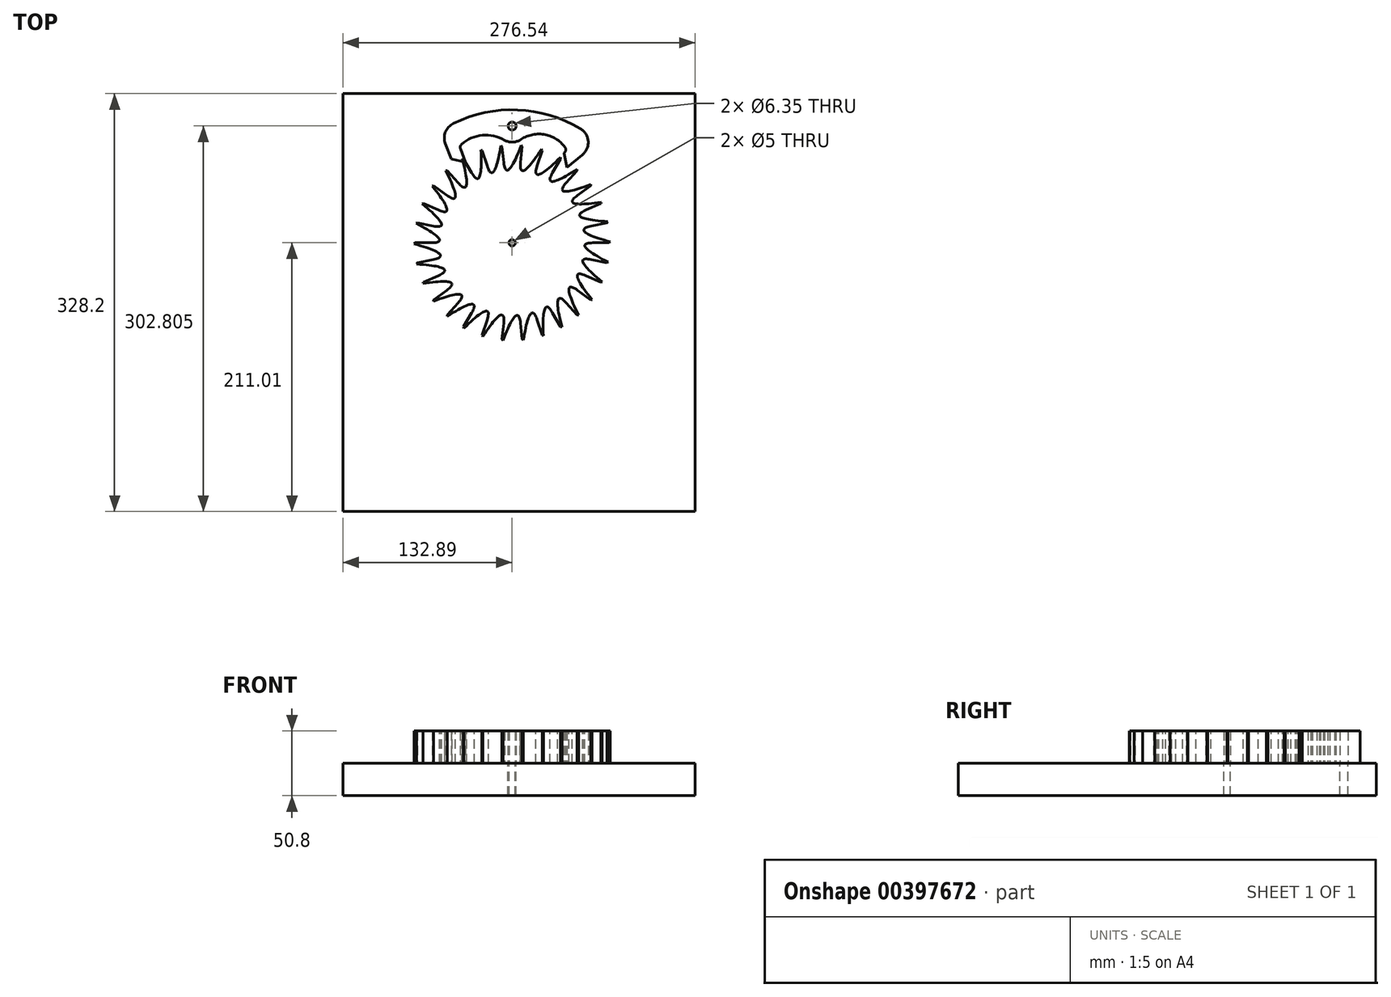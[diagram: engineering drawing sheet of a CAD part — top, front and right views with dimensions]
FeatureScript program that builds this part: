
annotation { "Feature Type Name" : "Feature", "Feature Type Description" : "" }
export const myFeature = defineFeature(function(context is Context, id is Id, definition is map)
    precondition{}
    {
        {
            var Q0;
            Q0=qCreatedBy(makeId("Top.planeOp"),FACE);
            var sketch = newSketch(context, id + "F0", { "sketchPlane" : qUnion([Q0])});
            skCircle(sketch, "E0", {"center": v(0, 0) * mm, "radius": 76.2 * mm, "construction": true});
            skCircle(sketch, "E1", {"center": v(0, 0) * mm, "radius": 95.25 * mm, "construction": true});
            skCircle(sketch, "E2", {"center": v(0, 0) * mm, "radius": 57.15 * mm, "construction": true});
            skLineSegment(sketch, "E3", {"start": v(0, 0) * mm, "end": v(-38.48, 66.66) * mm, "construction": true});
            skLineSegment(sketch, "E4", {"start": v(-104.67, 27.56) * mm, "end": v(65.84, 126) * mm, "construction": true});
            skLineSegment(sketch, "E5", {"start": v(0, 0) * mm, "end": v(-38.24, 42.47) * mm, "construction": true});
            skLineSegment(sketch, "E6", {"start": v(-96.61, 34.43) * mm, "end": v(96.61, 141.54) * mm, "construction": true});
            skPoint(sketch, "E7", {"position": v(0, 87.99) * mm});
            skPoint(sketch, "E7.positionSnap0", {"position": v(0, 87.99) * mm});
            skLineSegment(sketch, "E8", {"start": v(-38.1, 66) * mm, "end": v(-39.17, 66.28) * mm});
            skPoint(sketch, "E9", {"position": v(-42.49, 47.19) * mm});
            skPoint(sketch, "E10", {"position": v(-37.64, 60.11) * mm});
            skLineSegment(sketch, "E11.trimOffspring", {"start": v(-40.07, 69.4) * mm, "end": v(-47.63, 82.49) * mm});
            skEllipticalArc(sketch, "E12.trimOffspring", {});
            skLineSegment(sketch, "E13.trimOffspring", {"start": v(-42.49, 47.19) * mm, "end": v(-50.99, 56.63) * mm});
            skCircle(sketch, "E14", {"center": v(0, 0) * mm, "radius": 2.5 * mm});
            skLineSegment(sketch, "E15", {"start": v(0, 0) * mm, "end": v(61, 105.66) * mm, "construction": true});
            skLineSegment(sketch, "E16.1.0", {"start": v(-50.99, 56.63) * mm, "end": v(-52.1, 56.69) * mm});
            skEllipticalArc(sketch, "E16.1.1", {});
            skLineSegment(sketch, "E16.1.2", {"start": v(-51.37, 37.32) * mm, "end": v(-61.65, 44.79) * mm});
            skLineSegment(sketch, "E16.2.0", {"start": v(-61.65, 44.79) * mm, "end": v(-62.74, 44.62) * mm});
            skEllipticalArc(sketch, "E16.2.1", {});
            skLineSegment(sketch, "E16.2.2", {"start": v(-58.01, 25.83) * mm, "end": v(-69.61, 31) * mm});
            skEllipticalArc(sketch, "E17.3.3.0", {});
            skLineSegment(sketch, "E17.7.3.0", {"start": v(-62.11, 13.2) * mm, "end": v(-74.53, 15.84) * mm});
            skLineSegment(sketch, "E17.9.3.0", {"start": v(-69.61, 31) * mm, "end": v(-70.64, 30.6) * mm});
            skEllipticalArc(sketch, "E17.3.4.0", {});
            skLineSegment(sketch, "E17.7.4.0", {"start": v(-63.5, 0) * mm, "end": v(-76.2, 0) * mm});
            skLineSegment(sketch, "E17.9.4.0", {"start": v(-74.53, 15.84) * mm, "end": v(-75.46, 15.24) * mm});
            skEllipticalArc(sketch, "E17.3.5.0", {});
            skLineSegment(sketch, "E17.7.5.0", {"start": v(-62.11, -13.2) * mm, "end": v(-74.53, -15.84) * mm});
            skLineSegment(sketch, "E17.9.5.0", {"start": v(-76.2, 0) * mm, "end": v(-76.98, -0.78) * mm});
            skEllipticalArc(sketch, "E17.3.6.0", {});
            skLineSegment(sketch, "E17.7.6.0", {"start": v(-58.01, -25.83) * mm, "end": v(-69.61, -31) * mm});
            skLineSegment(sketch, "E17.9.6.0", {"start": v(-74.53, -15.84) * mm, "end": v(-75.14, -16.77) * mm});
            skEllipticalArc(sketch, "E17.3.7.0", {});
            skLineSegment(sketch, "E17.7.7.0", {"start": v(-51.37, -37.32) * mm, "end": v(-61.65, -44.79) * mm});
            skLineSegment(sketch, "E17.9.7.0", {"start": v(-69.61, -31) * mm, "end": v(-70, -32.03) * mm});
            skEllipticalArc(sketch, "E17.3.8.0", {});
            skLineSegment(sketch, "E17.7.8.0", {"start": v(-42.49, -47.19) * mm, "end": v(-50.99, -56.63) * mm});
            skLineSegment(sketch, "E17.9.8.0", {"start": v(-61.65, -44.79) * mm, "end": v(-61.82, -45.88) * mm});
            skEllipticalArc(sketch, "E17.3.9.0", {});
            skLineSegment(sketch, "E17.7.9.0", {"start": v(-31.75, -55) * mm, "end": v(-38.1, -66) * mm});
            skLineSegment(sketch, "E17.9.9.0", {"start": v(-50.99, -56.63) * mm, "end": v(-50.93, -57.73) * mm});
            skEllipticalArc(sketch, "E17.3.10.0", {});
            skLineSegment(sketch, "E17.7.10.0", {"start": v(-19.62, -60.4) * mm, "end": v(-23.55, -72.47) * mm});
            skLineSegment(sketch, "E17.9.10.0", {"start": v(-38.1, -66) * mm, "end": v(-37.81, -67.06) * mm});
            skEllipticalArc(sketch, "E17.3.11.0", {});
            skLineSegment(sketch, "E17.7.11.0", {"start": v(-6.64, -63.15) * mm, "end": v(-7.97, -75.78) * mm});
            skLineSegment(sketch, "E17.9.11.0", {"start": v(-23.55, -72.47) * mm, "end": v(-23.05, -73.46) * mm});
            skEllipticalArc(sketch, "E17.3.12.0", {});
            skLineSegment(sketch, "E17.7.12.0", {"start": v(6.64, -63.15) * mm, "end": v(7.97, -75.78) * mm});
            skLineSegment(sketch, "E17.9.12.0", {"start": v(-7.97, -75.78) * mm, "end": v(-7.27, -76.64) * mm});
            skEllipticalArc(sketch, "E17.3.13.0", {});
            skLineSegment(sketch, "E17.7.13.0", {"start": v(19.62, -60.4) * mm, "end": v(23.55, -72.47) * mm});
            skLineSegment(sketch, "E17.9.13.0", {"start": v(7.97, -75.78) * mm, "end": v(8.82, -76.48) * mm});
            skEllipticalArc(sketch, "E17.3.14.0", {});
            skLineSegment(sketch, "E17.7.14.0", {"start": v(31.75, -55) * mm, "end": v(38.1, -66) * mm});
            skLineSegment(sketch, "E17.9.14.0", {"start": v(23.55, -72.47) * mm, "end": v(24.53, -72.97) * mm});
            skEllipticalArc(sketch, "E18.3.15.0", {});
            skLineSegment(sketch, "E18.7.15.0", {"start": v(42.49, -47.19) * mm, "end": v(50.99, -56.63) * mm});
            skLineSegment(sketch, "E18.9.15.0", {"start": v(38.1, -66) * mm, "end": v(39.17, -66.28) * mm});
            skEllipticalArc(sketch, "E18.3.16.0", {});
            skLineSegment(sketch, "E18.7.16.0", {"start": v(51.37, -37.32) * mm, "end": v(61.65, -44.79) * mm});
            skLineSegment(sketch, "E18.9.16.0", {"start": v(50.99, -56.63) * mm, "end": v(52.1, -56.69) * mm});
            skEllipticalArc(sketch, "E18.3.17.0", {});
            skLineSegment(sketch, "E18.7.17.0", {"start": v(58.01, -25.83) * mm, "end": v(69.61, -31) * mm});
            skLineSegment(sketch, "E18.9.17.0", {"start": v(61.65, -44.79) * mm, "end": v(62.74, -44.62) * mm});
            skEllipticalArc(sketch, "E18.3.18.0", {});
            skLineSegment(sketch, "E18.7.18.0", {"start": v(62.11, -13.2) * mm, "end": v(74.53, -15.84) * mm});
            skLineSegment(sketch, "E18.9.18.0", {"start": v(69.61, -31) * mm, "end": v(70.64, -30.6) * mm});
            skEllipticalArc(sketch, "E18.3.19.0", {});
            skLineSegment(sketch, "E18.7.19.0", {"start": v(63.5, 0) * mm, "end": v(76.2, 0) * mm});
            skLineSegment(sketch, "E18.9.19.0", {"start": v(74.53, -15.84) * mm, "end": v(75.46, -15.24) * mm});
            skEllipticalArc(sketch, "E18.3.20.0", {});
            skLineSegment(sketch, "E18.7.20.0", {"start": v(62.11, 13.2) * mm, "end": v(74.53, 15.84) * mm});
            skLineSegment(sketch, "E18.9.20.0", {"start": v(76.2, 0) * mm, "end": v(76.98, 0.78) * mm});
            skEllipticalArc(sketch, "E18.3.21.0", {});
            skLineSegment(sketch, "E18.7.21.0", {"start": v(58.01, 25.83) * mm, "end": v(69.61, 31) * mm});
            skLineSegment(sketch, "E18.9.21.0", {"start": v(74.53, 15.84) * mm, "end": v(75.14, 16.77) * mm});
            skEllipticalArc(sketch, "E18.3.22.0", {});
            skLineSegment(sketch, "E18.7.22.0", {"start": v(51.37, 37.32) * mm, "end": v(61.65, 44.79) * mm});
            skLineSegment(sketch, "E18.9.22.0", {"start": v(69.61, 31) * mm, "end": v(70, 32.03) * mm});
            skEllipticalArc(sketch, "E18.3.23.0", {});
            skLineSegment(sketch, "E18.7.23.0", {"start": v(42.49, 47.19) * mm, "end": v(50.99, 56.63) * mm});
            skLineSegment(sketch, "E18.9.23.0", {"start": v(61.65, 44.79) * mm, "end": v(61.82, 45.88) * mm});
            skEllipticalArc(sketch, "E18.3.24.0", {});
            skLineSegment(sketch, "E18.7.24.0", {"start": v(31.75, 55) * mm, "end": v(38.1, 66) * mm});
            skLineSegment(sketch, "E18.9.24.0", {"start": v(50.99, 56.63) * mm, "end": v(50.93, 57.73) * mm});
            skEllipticalArc(sketch, "E18.3.25.0", {});
            skLineSegment(sketch, "E18.7.25.0", {"start": v(19.62, 60.4) * mm, "end": v(23.55, 72.47) * mm});
            skLineSegment(sketch, "E18.9.25.0", {"start": v(38.1, 66) * mm, "end": v(37.81, 67.06) * mm});
            skEllipticalArc(sketch, "E18.3.26.0", {});
            skLineSegment(sketch, "E18.7.26.0", {"start": v(6.64, 63.15) * mm, "end": v(7.97, 75.78) * mm});
            skLineSegment(sketch, "E18.9.26.0", {"start": v(23.55, 72.47) * mm, "end": v(23.05, 73.46) * mm});
            skEllipticalArc(sketch, "E18.3.27.0", {});
            skLineSegment(sketch, "E18.7.27.0", {"start": v(-6.64, 63.15) * mm, "end": v(-7.97, 75.78) * mm});
            skLineSegment(sketch, "E18.9.27.0", {"start": v(7.97, 75.78) * mm, "end": v(7.27, 76.64) * mm});
            skEllipticalArc(sketch, "E18.3.28.0", {});
            skLineSegment(sketch, "E18.7.28.0", {"start": v(-19.62, 60.4) * mm, "end": v(-23.55, 72.47) * mm});
            skLineSegment(sketch, "E18.9.28.0", {"start": v(-7.97, 75.78) * mm, "end": v(-8.82, 76.48) * mm});
            skEllipticalArc(sketch, "E18.3.29.0", {});
            skLineSegment(sketch, "E18.7.29.0", {"start": v(-31.75, 55) * mm, "end": v(-38.1, 66) * mm});
            skLineSegment(sketch, "E18.9.29.0", {"start": v(-23.55, 72.47) * mm, "end": v(-24.53, 72.97) * mm});
            const initialGuessF0  = {"E12.trimOffspring": [-0.16816268729673498, 0.34113311566798743, 0.40352375597021906, -0.9149691679874722, 0.32512873879015974, 0.019857114403106217, 6.099533507210712, 0.36648975676927714], "E16.1.1": [-0.23541349198471206, 0.29871554997316746, 0.5849385805037574, -0.8110775900234511, 0.32512873879015974, 0.019857114403106217, 6.0995335072107135, 0.3664897567692766], "E16.2.1": [-0.29237559743369124, 0.2432426813482785, 0.7407887822225573, -0.6717380293933201, 0.32512873879015974, 0.019857114403106217, 6.099533507210716, 0.36648975676927575], "E17.3.3.0": [-0.3365594863010441, 0.17713894034058497, 0.864262959459267, -0.5030402935220094, 0.32512873879015974, 0.019857114403106217, 6.0995335072107135, 0.36648975676927664], "E17.3.4.0": [-0.3660341106254456, 0.1032933776330654, 0.9499646981738034, -0.31235728296864607, 0.32512873879015974, 0.019857114403106217, 6.099533507210712, 0.366489756769277], "E17.3.5.0": [-0.3795112878889799, 0.024933398666362776, 0.994148421141772, -0.108022760293014, 0.32512873879015974, 0.019857114403106217, 6.099533507210712, 0.3664897567692774], "E17.3.6.0": [-0.3764020007745591, -0.05451628946578102, 0.9948830876524474, 0.10103287535813742, 0.32512873879015974, 0.019857114403106217, 6.099533507210713, 0.36648975676927614], "E17.3.7.0": [-0.35684214004909803, -0.1315833541500894, 0.9521365892539916, 0.30567288954661254, 0.32512873879015974, 0.019857114403106217, 6.09953350721071, 0.36648975676927764], "E17.3.8.0": [-0.3216865654849248, -0.20289959485105222, 0.8677771530468744, 0.49695353168064077, 0.32512873879015974, 0.019857114403106217, 6.099533507210713, 0.36648975676927675], "E17.3.9.0": [-0.2724717443856568, -0.26534814963674647, 0.7454916911948335, 0.6665149198326074, 0.32512873879015974, 0.019857114403106217, 6.099533507210709, 0.3664897567692777], "E17.3.10.0": [-0.21134860059224522, -0.3161997170016246, 0.5906246651715533, 0.806946407694458, 0.32512873879015974, 0.019857114403106217, 6.099533507210708, 0.3664897567692784], "E17.3.11.0": [-0.1409885087898473, -0.3532318394389483, 0.40994450714869024, 0.9121104653815882, 0.32512873879015974, 0.019857114403106217, 6.099533507210709, 0.3664897567692783], "E17.3.12.0": [-0.0644665426154071, -0.37482603549836785, 0.21134780703143413, 0.9774109189399328, 0.32512873879015974, 0.019857114403106217, 6.099533507210708, 0.36648975676927825], "E17.3.13.0": [0.014872920816119035, -0.38003853519163716, 0.0035141935876077833, 0.9999938252026503, 0.32512873879015974, 0.019857114403106217, 6.099533507210706, 0.36648975676927936], "E17.3.14.0": [0.09356236623978852, -0.36864152726981186, -0.20447300697896975, 0.9788722028012534, 0.32512873879015974, 0.019857114403106217, 6.099533507210706, 0.3664897567692789], "E18.3.15.0": [0.16816268729673456, -0.34113311566798726, -0.4035237559702191, 0.9149691679874721, 0.32512873879015974, 0.019857114403106217, 6.0995335072107055, 0.3664897567692796], "E18.3.16.0": [0.2354134919847116, -0.2987155499731673, -0.5849385805037571, 0.8110775900234511, 0.32512873879015974, 0.019857114403106217, 6.099533507210705, 0.3664897567692797], "E18.3.17.0": [0.2923755974336907, -0.2432426813482784, -0.7407887822225572, 0.6717380293933201, 0.32512873879015974, 0.019857114403106214, 6.099533507210705, 0.36648975676928064], "E18.3.18.0": [0.3365594863010437, -0.17713894034058492, -0.8642629594592669, 0.5030402935220095, 0.32512873879015974, 0.019857114403106217, 6.099533507210706, 0.36648975676927975], "E18.3.19.0": [0.36603411062544516, -0.10329337763306534, -0.9499646981738034, 0.31235728296864623, 0.32512873879015974, 0.019857114403106217, 6.099533507210705, 0.3664897567692802], "E18.3.20.0": [0.37951128788897953, -0.02493339866636276, -0.9941484211417722, 0.10802276029301414, 0.32512873879015974, 0.019857114403106217, 6.0995335072107055, 0.36648975676928014], "E18.3.21.0": [0.37640200077455865, 0.05451628946578116, -0.9948830876524474, -0.10103287535813729, 0.32512873879015974, 0.019857114403106217, 6.099533507210706, 0.3664897567692802], "E18.3.22.0": [0.35684214004909776, 0.13158335415008934, -0.9521365892539917, -0.3056728895466124, 0.32512873879015974, 0.019857114403106217, 6.0995335072107055, 0.36648975676928003], "E18.3.23.0": [0.32168656548492447, 0.20289959485105225, -0.8677771530468744, -0.4969535316806406, 0.32512873879015974, 0.019857114403106217, 6.099533507210707, 0.3664897567692799], "E18.3.24.0": [0.2724717443856564, 0.26534814963674663, -0.7454916911948336, -0.6665149198326072, 0.32512873879015974, 0.019857114403106217, 6.099533507210708, 0.36648975676928003], "E18.3.25.0": [0.211348600592245, 0.31619971700162464, -0.5906246651715534, -0.806946407694458, 0.32512873879015974, 0.019857114403106217, 6.099533507210707, 0.36648975676927903], "E18.3.26.0": [0.14098850878984698, 0.35323183943894854, -0.4099445071486904, -0.9121104653815882, 0.32512873879015974, 0.019857114403106217, 6.099533507210711, 0.36648975676927825], "E18.3.27.0": [0.06446654261540674, 0.374826035498368, -0.21134780703143421, -0.9774109189399326, 0.32512873879015974, 0.019857114403106217, 6.099533507210711, 0.36648975676927875], "E18.3.28.0": [-0.01487292081611923, 0.3800385351916374, -0.0035141935876079056, -0.9999938252026503, 0.32512873879015974, 0.019857114403106217, 6.099533507210711, 0.36648975676927703], "E18.3.29.0": [-0.09356236623978904, 0.368641527269812, 0.20447300697896967, -0.9788722028012535, 0.32512873879015974, 0.019857114403106217, 6.099533507210712, 0.36648975676927786]};
            skSetInitialGuess(sketch, initialGuessF0);
            skSolve(sketch);
        }
        {
            var Q0;
            Q0=qSketchRegion(id+"F0",true);
            extrude(context, id + "F1", {"entities" : qUnion([Q0]), "depth" : 25.4 * mm});
        }
        {
            var Q0;
            Q0=qCreatedBy(makeId("Top.planeOp"),FACE);
            var sketch = newSketch(context, id + "F2", { "sketchPlane" : qUnion([Q0])});
            skLineSegment(sketch, "E19", {"start": v(0, 0) * mm, "end": v(-100.8, 155.22) * mm, "construction": true});
            skLineSegment(sketch, "E20", {"start": v(0, 0) * mm, "end": v(100.8, 155.22) * mm, "construction": true});
            skLineSegment(sketch, "E21", {"start": v(0, 0) * mm, "end": v(-108.35, 149.14) * mm, "construction": true});
            skLineSegment(sketch, "E22", {"start": v(0, 0) * mm, "end": v(-92.17, 159.65) * mm, "construction": true});
            skLineSegment(sketch, "E23", {"start": v(0, 0) * mm, "end": v(86.35, 149.56) * mm, "construction": true});
            skLineSegment(sketch, "E24", {"start": v(0, 0) * mm, "end": v(101.51, 139.72) * mm, "construction": true});
            skCircle(sketch, "E25", {"center": v(0, 0) * mm, "radius": 76.99 * mm, "construction": true});
            skPoint(sketch, "E26.0", {"position": v(-8.82, 76.48) * mm});
            skLineSegment(sketch, "E27", {"start": v(-41.93, 64.57) * mm, "end": v(0, 91.8) * mm, "construction": true});
            skLineSegment(sketch, "E28", {"start": v(0, 91.8) * mm, "end": v(41.93, 64.57) * mm, "construction": true});
            skLineSegment(sketch, "E29", {"start": v(-47.82, 65.82) * mm, "end": v(-36.63, 63.44) * mm});
            skLineSegment(sketch, "E30", {"start": v(40.68, 70.46) * mm, "end": v(43.06, 59.26) * mm});
            skCircle(sketch, "E31", {"center": v(0, 91.8) * mm, "radius": 3.18 * mm});
            skLineSegment(sketch, "E32", {"start": v(-47.82, 65.82) * mm, "end": v(-52.42, 77.8) * mm});
            skLineSegment(sketch, "E33", {"start": v(43.06, 59.26) * mm, "end": v(55.03, 68.96) * mm});
            skLineSegment(sketch, "E34", {"start": v(40.68, 70.46) * mm, "end": v(40.94, 70.67) * mm});
            skLineSegment(sketch, "E35", {"start": v(-36.63, 63.44) * mm, "end": v(-40.61, 73.82) * mm});
            skArc(sketch, "E36", {"start": v(53.54, 89.73) * mm, "mid": v(4.2, 104.41) * mm, "end": v(-46.17, 93.74) * mm});
            skArc(sketch, "E37", {"start": v(-5.99, 80.6) * mm, "mid": v(0, 79.1) * mm, "end": v(5.99, 80.6) * mm});
            skArc(sketch, "E38.trimOffspring", {"start": v(-5.99, 80.6) * mm, "mid": v(-23.42, 84.52) * mm, "end": v(-39.77, 77.32) * mm});
            skArc(sketch, "E39.trimOffspring", {"start": v(41.51, 75) * mm, "mid": v(24.9, 85.16) * mm, "end": v(5.99, 80.6) * mm});
            skPoint(sketch, "E40.visualSharp", {"position": v(-56.34, 88) * mm});
            skArc(sketch, "E40.filletArc", {"start": v(-46.17, 93.74) * mm, "mid": v(-52.39, 86.98) * mm, "end": v(-52.42, 77.8) * mm});
            skPoint(sketch, "E41.visualSharp", {"position": v(67.93, 79.4) * mm});
            skArc(sketch, "E41.filletArc", {"start": v(55.03, 68.96) * mm, "mid": v(59.7, 79.73) * mm, "end": v(53.54, 89.73) * mm});
            skPoint(sketch, "E42.visualSharp", {"position": v(-41.36, 75.78) * mm});
            skArc(sketch, "E42.filletArc", {"start": v(-39.77, 77.32) * mm, "mid": v(-40.74, 75.7) * mm, "end": v(-40.61, 73.82) * mm});
            skPoint(sketch, "E43.visualSharp", {"position": v(43.14, 72.45) * mm});
            skArc(sketch, "E43.filletArc", {"start": v(40.94, 70.67) * mm, "mid": v(42.1, 72.72) * mm, "end": v(41.51, 75) * mm});
            skSolve(sketch);
        }
        {
            var Q0;
            Q0=makeQuery(id+"F2.imprint","IMPRINT",FACE,{"disambiguationData":[TD([[makeQuery(id+"F2.imprint","IMPRINT",EDGE,{"derivedFrom":sQuery(id+"F2.wireOp",EDGE,"E29")}),1.0]])]});
            extrude(context, id + "F3", {"entities" : qUnion([Q0]), "depth" : 25.4 * mm});
        }
        {
            var Q0;
            Q0=qCreatedBy(makeId("Top.planeOp"),FACE);
            var sketch = newSketch(context, id + "F4", { "sketchPlane" : qUnion([Q0])});
            skLineSegment(sketch, "E44.bottom", {"start": v(-132.9, 117.2) * mm, "end": v(143.65, 117.2) * mm});
            skLineSegment(sketch, "E44.top", {"start": v(-132.9, -211.01) * mm, "end": v(143.65, -211.01) * mm});
            skLineSegment(sketch, "E44.left", {"start": v(-132.9, 117.2) * mm, "end": v(-132.9, -211.01) * mm});
            skLineSegment(sketch, "E44.right", {"start": v(143.65, 117.2) * mm, "end": v(143.65, -211.01) * mm});
            skCircle(sketch, "E45.0", {"center": v(0, 91.8) * mm, "radius": 3.18 * mm});
            skCircle(sketch, "E46.0", {"center": v(0, 0) * mm, "radius": 2.5 * mm});
            skSolve(sketch);
        }
        {
            var Q0;
            Q0=makeQuery(id+"F4.imprint","IMPRINT",FACE,{"disambiguationData":[TD([[makeQuery(id+"F4.imprint","IMPRINT",EDGE,{"derivedFrom":sQuery(id+"F4.wireOp",EDGE,"E44.bottom")}),-1.0]])]});
            extrude(context, id + "F5", {"entities" : qUnion([Q0]), "oppositeDirection" : true, "depth" : 25.4 * mm});
        }
    });
